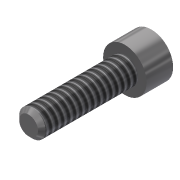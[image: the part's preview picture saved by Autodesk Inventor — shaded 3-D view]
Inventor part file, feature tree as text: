
AUTODESK INVENTOR PART (.ipt)
format: ipt  version: 2013 (Build 170138000, 138)  size: 103,424 bytes
history: native  units: in
note: dims shown in document units (in); Inventor stores cm internally (conversion verified against a paired STEP export)
features: extrude x3, sketch x3, thread x1, chamfer x1
ambient origin geometry x8: Origin, YZ Plane, XZ Plane, XY Plane, X Axis, Y Axis, Z Axis, Center Point
bodies: Solid1 (feature_tree)
feature tree (8):
  extrude  "Extrusion1"  Depth=0.5in TaperAngle=0.0deg
  extrude  "Extrusion2"  Depth=0.138in TaperAngle=0.0deg
  extrude  "Extrusion3"  Depth=0.069in TaperAngle=0.0deg
  thread  "Thread1"  [1 undecoded]
  chamfer  "Chamfer1"  Distance=0.02in Angle=45.0deg
  sketch  "Sketch1"  dims[d0=0.138in d1=0.5in d2=0.0in]
  sketch  "Sketch2"  dims[d3=0.226in d4=0.138in d5=0.0in]
  sketch  "Sketch3"  dims[d6=0.1094in d7=0.069in d8=0.0in d9=1.0in d10=0.0in d11=0.02in d12=0.125in d13=45.0deg]
note: 1 required parameter value undecoded (feature->parameter linkage not recoverable at this tier; creation-order binding heuristic only, values carry confidence <= 0.55)
